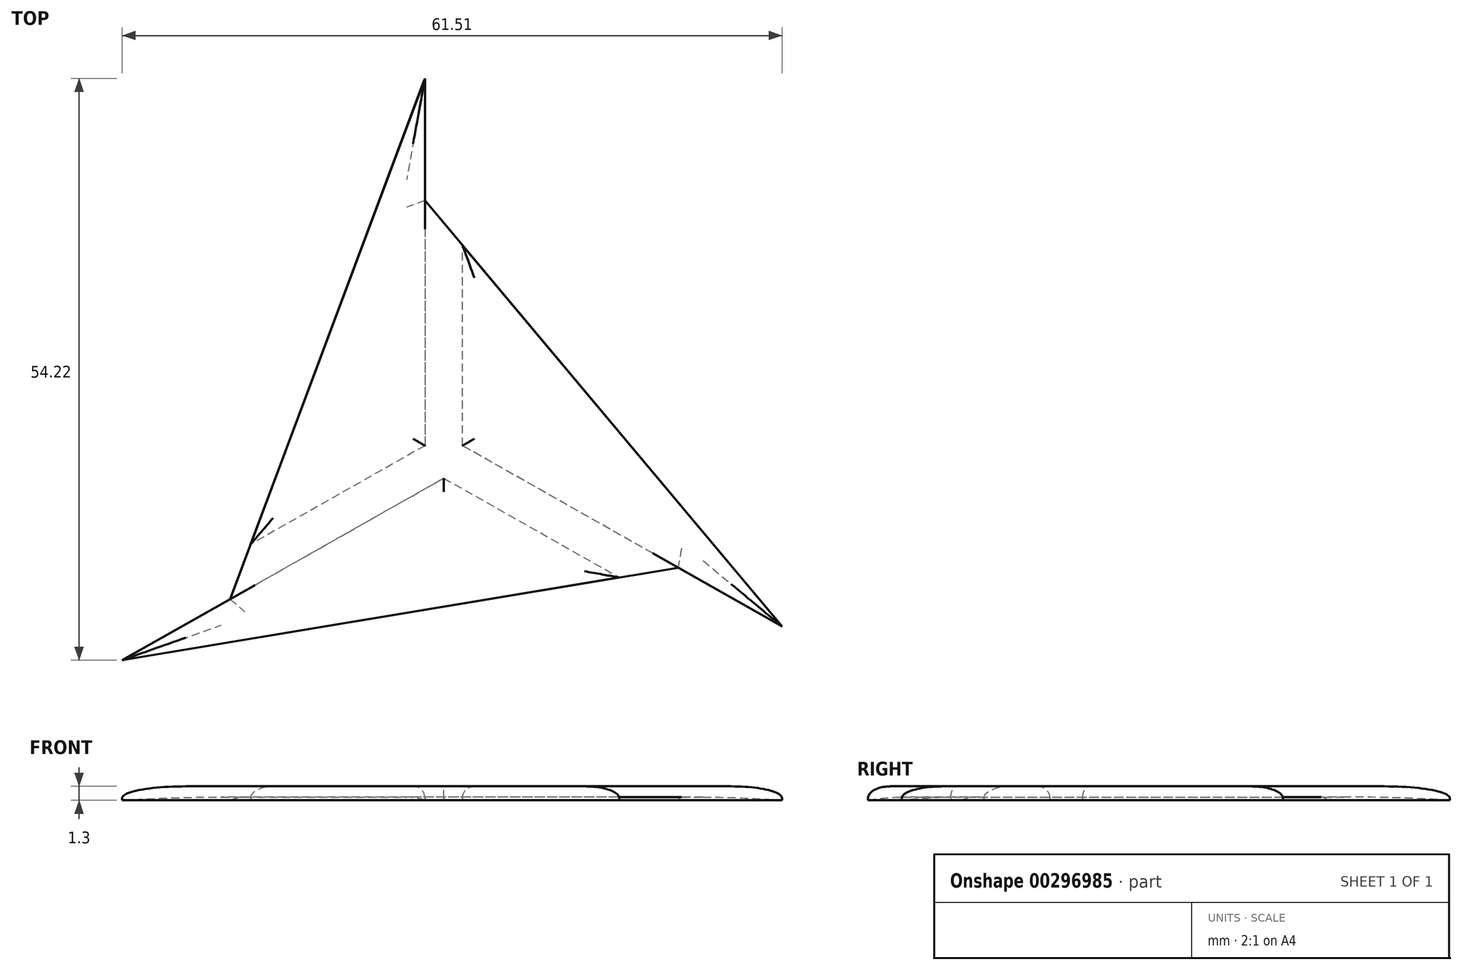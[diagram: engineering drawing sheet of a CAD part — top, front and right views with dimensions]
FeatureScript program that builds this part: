
annotation { "Feature Type Name" : "Feature", "Feature Type Description" : "" }
export const myFeature = defineFeature(function(context is Context, id is Id, definition is map)
    precondition{}
    {
        {
            var Q0;
            Q0=qCreatedBy(makeId("Top.planeOp"),FACE);
            var sketch = newSketch(context, id + "F0", { "sketchPlane" : qUnion([Q0])});
            skLineSegment(sketch, "E0.0", {"start": v(-40.27, 11.94) * mm, "end": v(-24.02, 55.35) * mm});
            skLineSegment(sketch, "E0.1", {"start": v(-24.02, 21.13) * mm, "end": v(-40.27, 11.94) * mm});
            skLineSegment(sketch, "E0.2", {"start": v(-24.02, 55.35) * mm, "end": v(-24.02, 21.13) * mm});
            skLineSegment(sketch, "E1.0", {"start": v(-20.52, 39.8) * mm, "end": v(9.26, 4.28) * mm});
            skLineSegment(sketch, "E1.1", {"start": v(-20.52, 21.13) * mm, "end": v(-20.52, 39.8) * mm});
            skLineSegment(sketch, "E1.2", {"start": v(9.26, 4.28) * mm, "end": v(-20.52, 21.13) * mm});
            skLineSegment(sketch, "E2.0", {"start": v(-5.92, 8.85) * mm, "end": v(-52.25, 1.13) * mm});
            skLineSegment(sketch, "E2.1", {"start": v(-22.27, 18.1) * mm, "end": v(-5.92, 8.85) * mm});
            skLineSegment(sketch, "E2.2", {"start": v(-52.25, 1.13) * mm, "end": v(-22.27, 18.1) * mm});
            skSolve(sketch);
        }
        {
            var Q0;
            Q0 = qSketchRegion(id + "F0", true);
            extrude(context, id + "F1", {"entities" : qUnion([Q0]), "depth" : 1.3 * mm, "offsetDistance" : 25 * mm});
        }
        {
            var Q0;
            Q0=makeQuery(id+"F1.opExtrude","CAP_FACE",FACE,{"disambiguationData":[OSD([sQuery(id+"F0.wireOp",EDGE,"E0.0"),sQuery(id+"F0.wireOp",EDGE,"E0.1"),sQuery(id+"F0.wireOp",EDGE,"E0.2")])],"isStart":false});
            var Q1;
            Q1=makeQuery(id+"F1.opExtrude","CAP_FACE",FACE,{"disambiguationData":[OSD([sQuery(id+"F0.wireOp",EDGE,"E1.0"),sQuery(id+"F0.wireOp",EDGE,"E1.1"),sQuery(id+"F0.wireOp",EDGE,"E1.2")])],"isStart":false});
            var Q2;
            Q2=makeQuery(id+"F1.opExtrude","CAP_FACE",FACE,{"disambiguationData":[OSD([sQuery(id+"F0.wireOp",EDGE,"E2.0"),sQuery(id+"F0.wireOp",EDGE,"E2.1"),sQuery(id+"F0.wireOp",EDGE,"E2.2")])],"isStart":false});
            fillet(context, id + "F2", {"entities" : qUnion([Q0, Q1, Q2]), "radius" : 1.1 * mm, "tangentPropagation" : true, "allowEdgeOverflow" : false});
        }
        {
            var Q0;
            Q0=makeQuery(id+"F1.opExtrude","CAP_FACE",FACE,{"disambiguationData":[OSD([sQuery(id+"F0.wireOp",EDGE,"E1.0"),sQuery(id+"F0.wireOp",EDGE,"E1.1"),sQuery(id+"F0.wireOp",EDGE,"E1.2")])],"isStart":true});
            var sketch = newSketch(context, id + "F3", { "sketchPlane" : qUnion([Q0])});
            skLineSegment(sketch, "E3", {"start": v(9.26, -4.28) * mm, "end": v(-20.52, -39.8) * mm});
            skLineSegment(sketch, "E4", {"start": v(-20.52, -39.8) * mm, "end": v(-24.02, -43.97) * mm});
            skLineSegment(sketch, "E5", {"start": v(-24.02, -43.97) * mm, "end": v(-24.02, -55.35) * mm});
            skLineSegment(sketch, "E6", {"start": v(-24.02, -55.35) * mm, "end": v(-42.18, -6.82) * mm});
            skLineSegment(sketch, "E7", {"start": v(-42.18, -6.82) * mm, "end": v(-52.25, -1.13) * mm});
            skLineSegment(sketch, "E8", {"start": v(-52.25, -1.13) * mm, "end": v(-0.44, -9.76) * mm});
            skLineSegment(sketch, "E9", {"start": v(-0.44, -9.76) * mm, "end": v(9.26, -4.28) * mm});
            skSolve(sketch);
        }
        {
            var Q0;
            Q0 = qSketchRegion(id + "F3", true);
            extrude(context, id + "F4", {"entities" : qUnion([Q0]), "oppositeDirection" : true, "depth" : 0.3 * mm, "offsetDistance" : 25 * mm});
        }
        {
            var Q0;
            Q0=makeQuery(id+"F4.opExtrude","CAP_FACE",FACE,{"disambiguationData":[OSD([sQuery(id+"F3.wireOp",EDGE,"E3"),sQuery(id+"F3.wireOp",EDGE,"E4"),sQuery(id+"F3.wireOp",EDGE,"E5"),sQuery(id+"F3.wireOp",EDGE,"E6"),sQuery(id+"F3.wireOp",EDGE,"E7"),sQuery(id+"F3.wireOp",EDGE,"E8"),sQuery(id+"F3.wireOp",EDGE,"E9")])],"isStart":false});
            fillet(context, id + "F5", {"entities" : qUnion([Q0]), "radius" : 5 * mm, "tangentPropagation" : true, "allowEdgeOverflow" : false});
        }
    });
